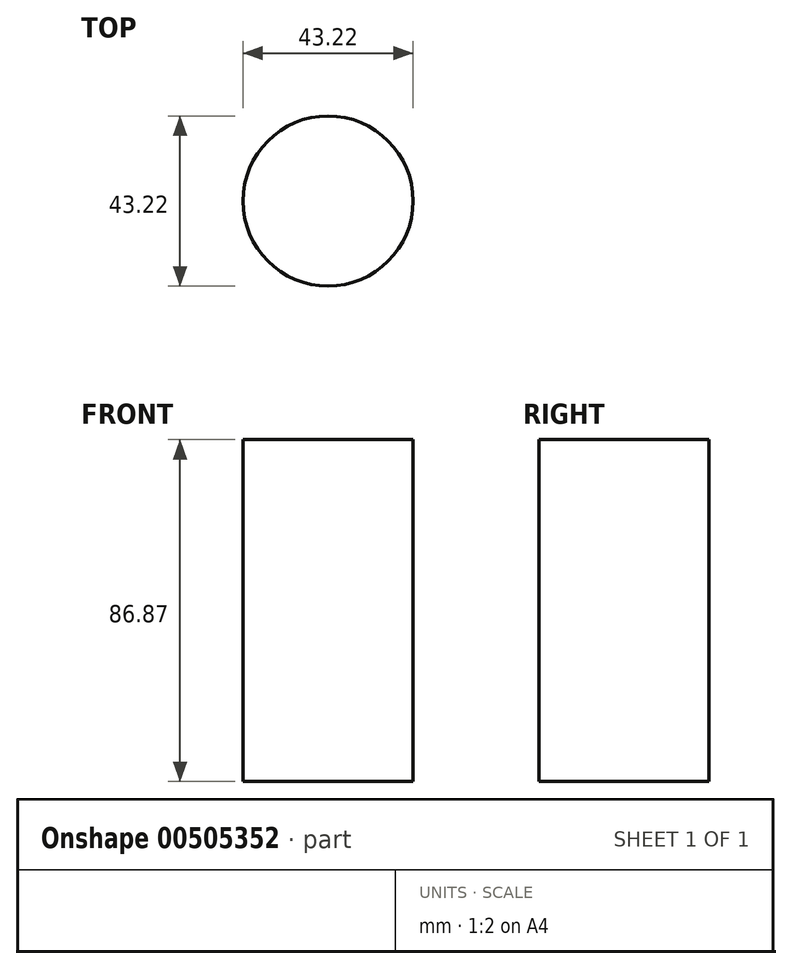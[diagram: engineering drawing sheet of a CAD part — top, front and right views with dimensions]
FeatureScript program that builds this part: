
annotation { "Feature Type Name" : "Feature", "Feature Type Description" : "" }
export const myFeature = defineFeature(function(context is Context, id is Id, definition is map)
    precondition{}
    {
        {
            var Q0;
            Q0=qCreatedBy(makeId("Top.planeOp"),FACE);
            var sketch = newSketch(context, id + "F0", { "sketchPlane" : qUnion([Q0])});
            skCircle(sketch, "E0", {"center": v(0, 0) * mm, "radius": 21.6 * mm});
            skSolve(sketch);
        }
        {
            var Q0;
            Q0=makeQuery(id+"F0.imprint","IMPRINT",FACE,{"disambiguationData":[TD([[makeQuery(id+"F0.imprint","IMPRINT",EDGE,{"derivedFrom":sQuery(id+"F0.wireOp",EDGE,"E0")}),1.0]])]});
            extrude(context, id + "F1", {"entities" : qUnion([Q0]), "depth" : 86.87 * mm});
        }
    });
